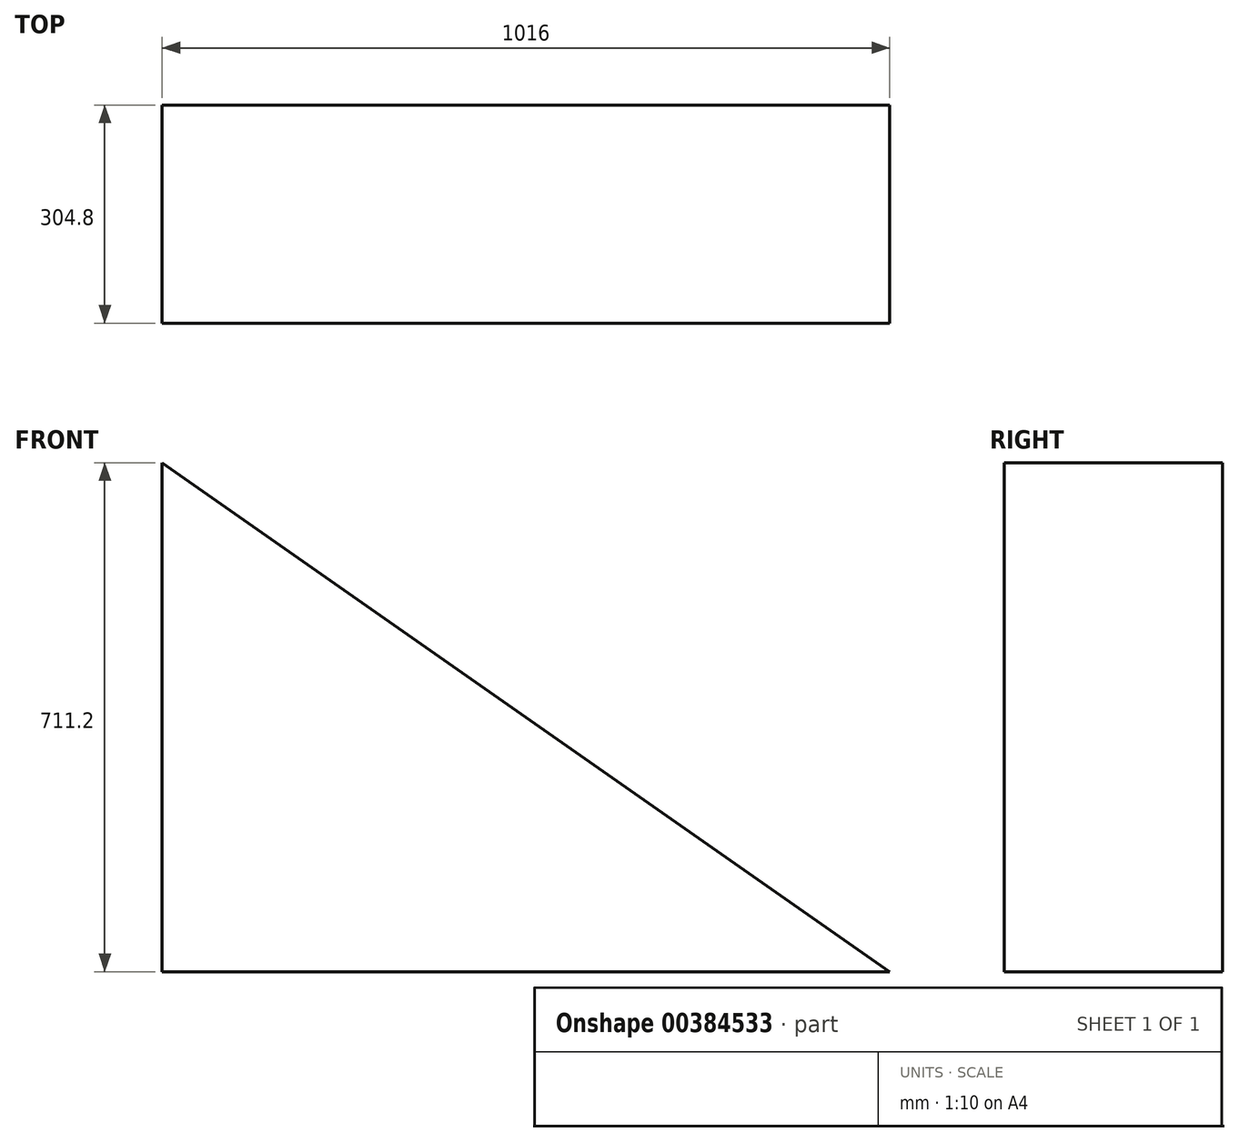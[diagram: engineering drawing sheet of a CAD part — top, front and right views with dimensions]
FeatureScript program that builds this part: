
annotation { "Feature Type Name" : "Feature", "Feature Type Description" : "" }
export const myFeature = defineFeature(function(context is Context, id is Id, definition is map)
    precondition{}
    {
        {
            var Q0;
            Q0=qCreatedBy(makeId("Front.planeOp"),FACE);
            var sketch = newSketch(context, id + "F0", { "sketchPlane" : qUnion([Q0])});
            skLineSegment(sketch, "E0", {"start": v(0, 0) * mm, "end": v(0, 711.2) * mm});
            skLineSegment(sketch, "E1", {"start": v(0, 711.2) * mm, "end": v(1016, 0) * mm});
            skLineSegment(sketch, "E2", {"start": v(1016, 0) * mm, "end": v(0, 0) * mm});
            skSolve(sketch);
        }
        {
            var Q0;
            Q0 = qSketchRegion(id + "F0", true);
            extrude(context, id + "F1", {"entities" : qUnion([Q0]), "depth" : 304.8 * mm});
        }
    });
